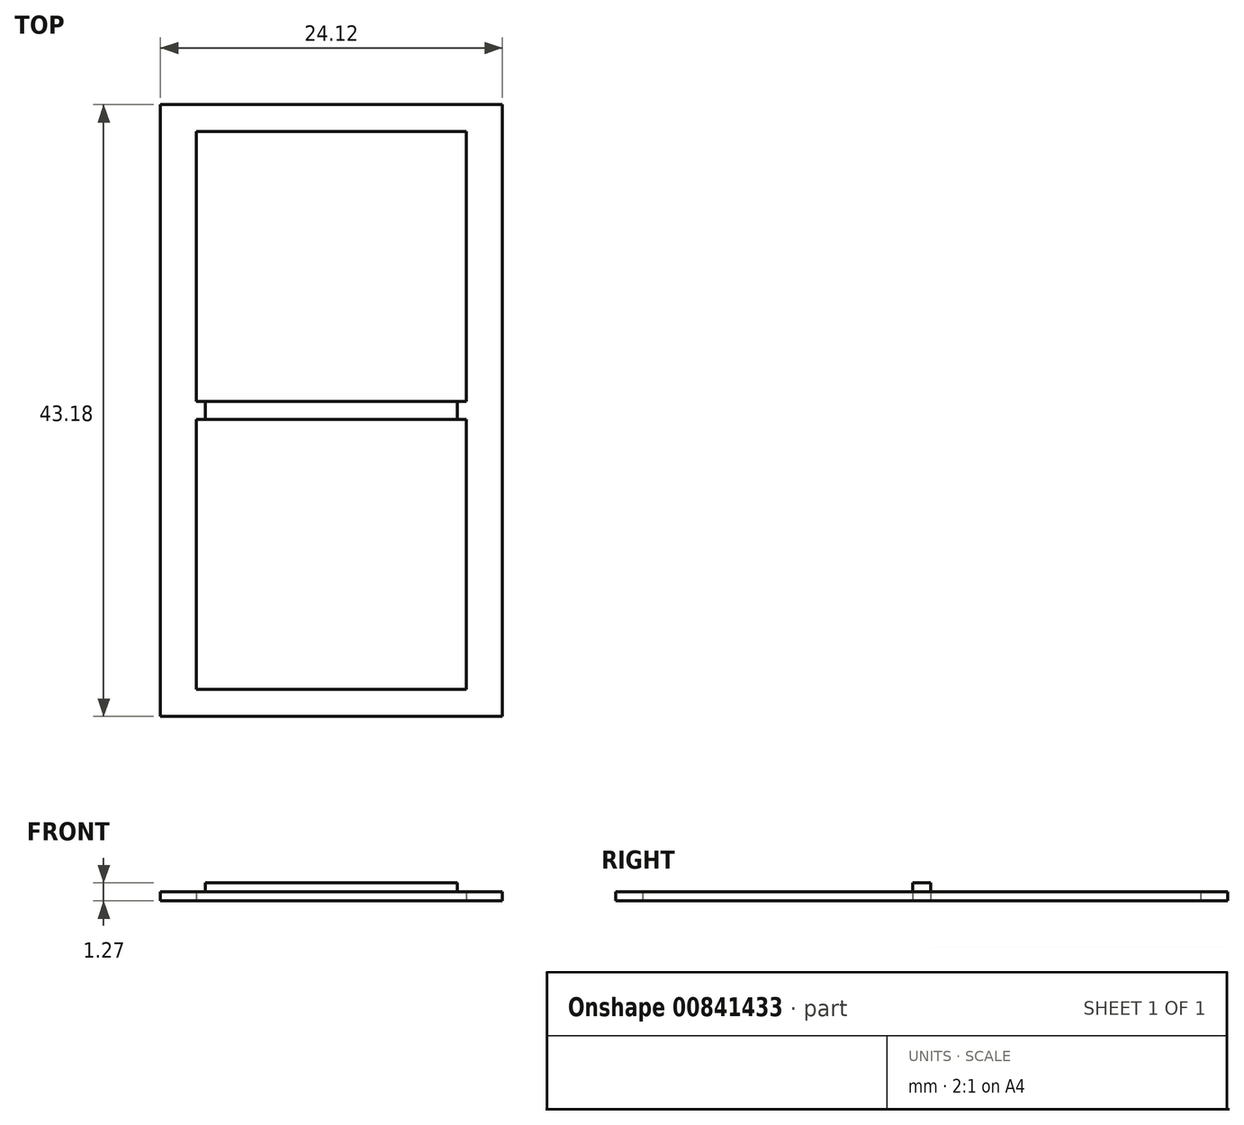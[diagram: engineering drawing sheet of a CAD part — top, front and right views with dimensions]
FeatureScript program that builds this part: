
annotation { "Feature Type Name" : "Feature", "Feature Type Description" : "" }
export const myFeature = defineFeature(function(context is Context, id is Id, definition is map)
    precondition{}
    {
        {
            var Q0;
            Q0=qCreatedBy(makeId("Top.planeOp"),FACE);
            var sketch = newSketch(context, id + "F0", { "sketchPlane" : qUnion([Q0])});
            skLineSegment(sketch, "E0.bottom", {"start": v(12.07, 21.59) * mm, "end": v(-12.06, 21.59) * mm});
            skLineSegment(sketch, "E0.top", {"start": v(12.06, -21.59) * mm, "end": v(-12.07, -21.59) * mm});
            skLineSegment(sketch, "E0.left", {"start": v(12.07, 21.59) * mm, "end": v(12.06, -21.59) * mm});
            skLineSegment(sketch, "E0.right", {"start": v(-12.06, 21.59) * mm, "end": v(-12.07, -21.59) * mm});
            skPoint(sketch, "E0.middle", {"position": v(0, 0) * mm});
            skLineSegment(sketch, "E1.bottom", {"start": v(9.53, -0.64) * mm, "end": v(-9.53, -0.64) * mm});
            skLineSegment(sketch, "E1.top", {"start": v(9.53, -19.69) * mm, "end": v(-9.53, -19.69) * mm});
            skLineSegment(sketch, "E1.left", {"start": v(9.53, -0.64) * mm, "end": v(9.53, -19.69) * mm});
            skLineSegment(sketch, "E1.right", {"start": v(-9.53, -0.64) * mm, "end": v(-9.53, -19.69) * mm});
            skLineSegment(sketch, "E2.bottom", {"start": v(9.53, 0.64) * mm, "end": v(-9.52, 0.63) * mm});
            skLineSegment(sketch, "E2.top", {"start": v(9.52, 19.69) * mm, "end": v(-9.53, 19.69) * mm});
            skLineSegment(sketch, "E2.left", {"start": v(9.53, 0.64) * mm, "end": v(9.53, 19.69) * mm});
            skLineSegment(sketch, "E2.right", {"start": v(-9.52, 0.63) * mm, "end": v(-9.53, 19.69) * mm});
            skLineSegment(sketch, "E3.bottom", {"start": v(8.9, 0.64) * mm, "end": v(-8.9, 0.64) * mm});
            skLineSegment(sketch, "E3.top", {"start": v(8.9, -0.64) * mm, "end": v(-8.9, -0.64) * mm});
            skLineSegment(sketch, "E3.left", {"start": v(8.9, 0.64) * mm, "end": v(8.9, -0.63) * mm});
            skLineSegment(sketch, "E3.right", {"start": v(-8.9, 0.63) * mm, "end": v(-8.9, -0.64) * mm});
            skSolve(sketch);
        }
        {
            var Q0;
            Q0=makeQuery(id+"F0.imprint","IMPRINT",FACE,{"disambiguationData":[TD([[makeQuery(id+"F0.imprint","IMPRINT",EDGE,{"derivedFrom":sQuery(id+"F0.wireOp",EDGE,"E0.bottom")}),1.0]])]});
            extrude(context, id + "F1", {"entities" : qUnion([Q0]), "depth" : 0.64 * mm, "offsetDistance" : 25.4 * mm});
        }
        {
            var Q0;
            {var subQ0=sQuery(id+"F0.wireOp",EDGE,"E3.left");Q0=makeQuery(id+"F0.imprint","IMPRINT",FACE,{"disambiguationData":[TD([[makeQuery(id+"F0.imprint","IMPRINT",EDGE,{"derivedFrom":subQ0}),-1.0]])]});}
            extrude(context, id + "F2", {"entities" : qUnion([Q0]), "operationType" : NewBodyOperationType.ADD, "depth" : 1.27 * mm, "offsetDistance" : 25.4 * mm});
        }
    });
